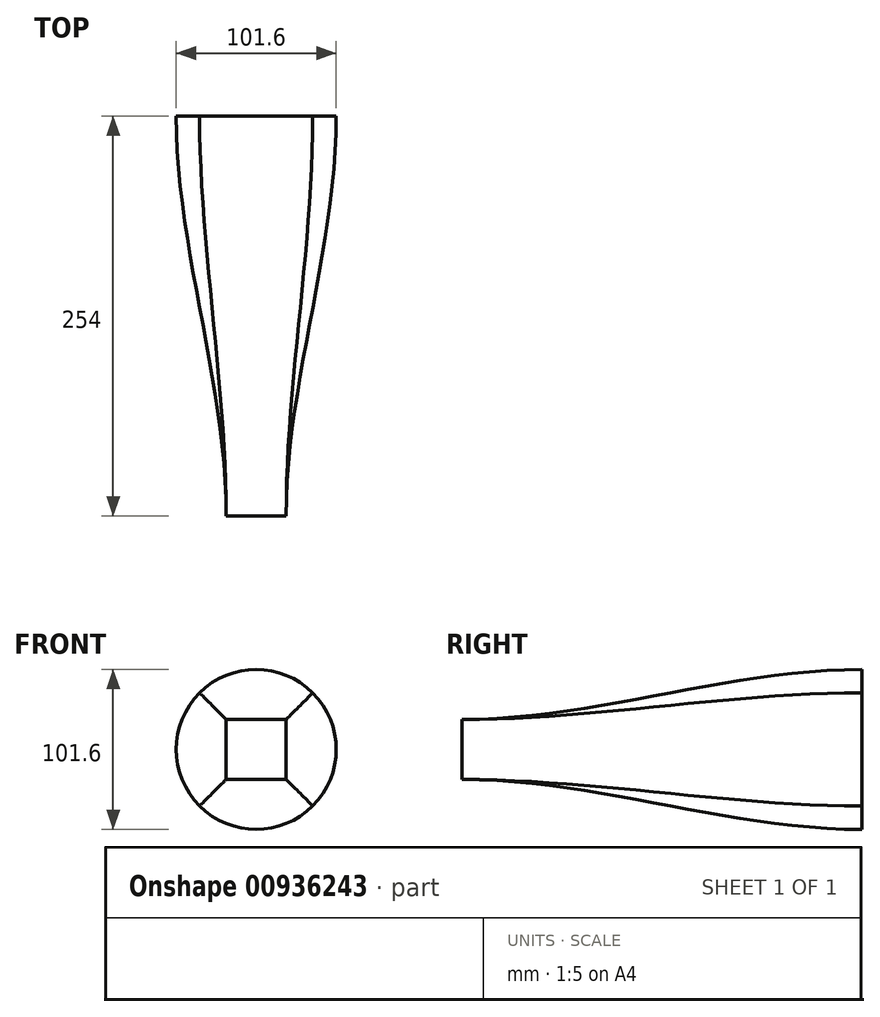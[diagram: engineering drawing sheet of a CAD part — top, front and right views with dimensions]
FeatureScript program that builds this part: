
annotation { "Feature Type Name" : "Feature", "Feature Type Description" : "" }
export const myFeature = defineFeature(function(context is Context, id is Id, definition is map)
    precondition{}
    {
        {
            var Q0;
            Q0=qCreatedBy(makeId("Front.planeOp"),FACE);
            var sketch = newSketch(context, id + "F0", { "sketchPlane" : qUnion([Q0])});
            skCircle(sketch, "E0", {"center": v(0, 0) * mm, "radius": 50.8 * mm});
            skSolve(sketch);
        }
        {
            var Q0;
            Q0=makeQuery(id+"F0.imprint","IMPRINT",FACE,{"disambiguationData":[TD([[makeQuery(id+"F0.imprint","IMPRINT",EDGE,{"derivedFrom":sQuery(id+"F0.wireOp",EDGE,"E0")}),1.0]])]});
            cPlane(context, id + "F1", {"entities" : qUnion([Q0]), "cplaneType" : CPlaneType.OFFSET, "offset" : 254 * mm, "width" : 152.4 * mm, "height" : 152.4 * mm});
        }
        {
            var Q0;
            Q0=qCreatedBy(id+"F1.planeOp",FACE);
            var sketch = newSketch(context, id + "F2", { "sketchPlane" : qUnion([Q0])});
            skLineSegment(sketch, "E1.bottom", {"start": v(19.05, 19.05) * mm, "end": v(-19.05, 19.05) * mm});
            skLineSegment(sketch, "E1.top", {"start": v(19.05, -19.05) * mm, "end": v(-19.05, -19.05) * mm});
            skLineSegment(sketch, "E1.left", {"start": v(19.05, 19.05) * mm, "end": v(19.05, -19.05) * mm});
            skLineSegment(sketch, "E1.right", {"start": v(-19.05, 19.05) * mm, "end": v(-19.05, -19.05) * mm});
            skPoint(sketch, "E1.middle", {"position": v(0, 0) * mm});
            skSolve(sketch);
        }
        {
            var Q0;
            Q0=makeQuery(id+"F0.imprint","IMPRINT",FACE,{"disambiguationData":[TD([[makeQuery(id+"F0.imprint","IMPRINT",EDGE,{"derivedFrom":sQuery(id+"F0.wireOp",EDGE,"E0")}),1.0]])]});
            var Q1;
            Q1=makeQuery(id+"F2.imprint","IMPRINT",FACE,{"disambiguationData":[TD([[makeQuery(id+"F2.imprint","IMPRINT",EDGE,{"derivedFrom":sQuery(id+"F2.wireOp",EDGE,"E1.bottom")}),1.0]])]});
            loft(context, id + "F3", {"sheetProfilesArray" : [{ "sheetProfileEntities" : qUnion([Q0]) }, { "sheetProfileEntities" : qUnion([Q1]) }], "startCondition" : LoftEndDerivativeType.NORMAL_TO_PROFILE, "startMagnitude" : 1, "endCondition" : LoftEndDerivativeType.NORMAL_TO_PROFILE, "endMagnitude" : 1});
        }
    });
